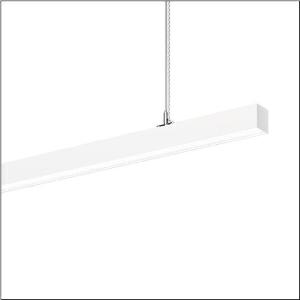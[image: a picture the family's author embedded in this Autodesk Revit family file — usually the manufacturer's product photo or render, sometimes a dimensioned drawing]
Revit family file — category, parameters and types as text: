
# Revit family: silica_r__21_51mx33db49wb_5808
name_source: partatom
category: Lighting Fixtures
units: mm (PartAtom-declared; Revit-internal decimal feet)

## family parameters
Cut with Voids When Loaded = No
Host = Face
Light Source = No
Part Type = Normal
Room Calculation Point = No
Round Connector Dimension = Use Diameter
Shared = No

## types (1)
- --- (1 x LED, 7390 lm, 48.3 W, 4000K)
    Apparent Load = 48 VA
    CIE Flux Codes = 78 96 99 55 100
    Color Rendering = 80
    Color Temperature = 4000K
    Default Elevation = 1800 mm
    Description = Silica® 21, office luminaire, primary optical cover: prismatic diffuser, of PMMA, CAT 2 (L<= 3000cd/m²), light emission: direct/indirect distribution, primary light characteristic: symmetric, installation type: suspended mounting, LED, rated luminous flux: 7.390lm, luminous efficacy: 153lm/W, light colour: 840, colour temperature: 4000K, with terminal, 3+2-pole, max. 2.5mm², mains connection: 220..240V, AC, 50/60Hz, rated input power: 48.3W, luminaire housing, of aluminium, traffic white (RAL 9016), length: 1.504mm, width: 53mm, height: 53mm, protection rating (complete): IP20, insulation class (complete): insulation class I (protective earthing), certification: CE, permissible operating ambient temperature: 0..+35°C, standard: EN 50419, packaging unit: 1 piece
    Height = 53 mm
    Lamp = 1 x LED
    Lamp Light Flux = 7390 lm
    Lamp Power = 48.3 W
    Lamp count = 1
    Length = 1504 mm
    Luminous efficacy = 153 lm/W
    Manufacturer = Siteco
    ModVariant = No
    Model = 51MX33DB49WB
    Mounting Place = Ceiling
    Mounting Type = Pendant
    Number of Poles = 1
    OnlyDefault = Yes
    Power Factor = 1
    Product Name = Silica® 21
    Product group = office luminaire | ceiling pendant
    ProductGroupID = 902
    Protection Class = Protection class I
    Protection Degree = IP 20
    RLX_Detail_Level = 1
    RLX_Emergency_Light_Flux = 0 lm
    RLX_Emergency_Type = 0
    RLX_Emergency_Type_DB = No
    RlxData = <blob elided: 21569 chars, md5=51fb628b>
    Socket = socket
    Standby Power = 0 W
    System Light Flux = 7390 lm
    System Power = 48 W
    Type Comments = factory setting: luminous flux: 100 % | dim-lin: 254 | 323 mA
    Type Image = l_1297784.jpg
    URL = http://relux.com
    VarID = @adj_048569
    Voltage = 0 V
    Weight = 0.00 kg
    Width = 53 mm

## geometry (parser evidence)
native form markers: Blend x4, Sweep x12
no freeform markers — native parametric forms only
